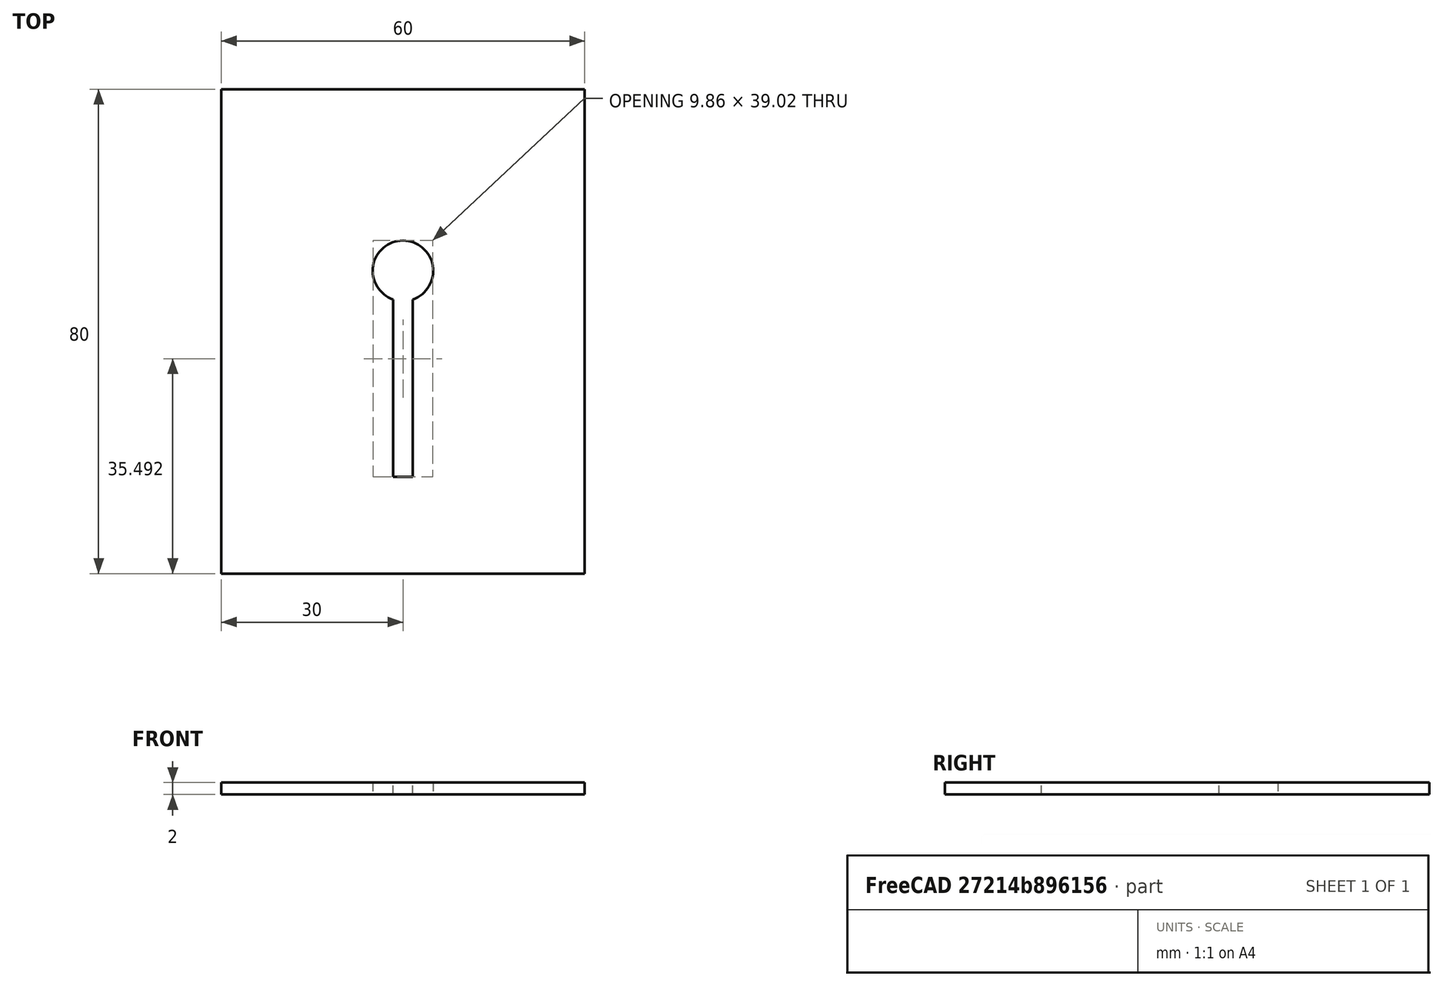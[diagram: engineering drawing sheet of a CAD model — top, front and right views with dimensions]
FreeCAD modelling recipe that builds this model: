
FCSTD DOCUMENT  (FreeCAD 0.15R4671 (Git))
Label: example 3
License: All rights reserved
LicenseURL: http://en.wikipedia.org/wiki/All_rights_reserved
objects: Sketcher::SketchObject×1, PartDesign::Pad×1
note: 3 computed .brp shape members not serialized (recipe doc carries the construction recipe); baked Part::Feature solids carry a one-line shape summary decoded from their .brp

FEATURE [Sketcher::SketchObject] Sketch  label="front plate sketch"
  Placement = pos=(0,0,32) rot=(0,0,1;0rad)
  sketch-geometry (8):
    g0: LineSegment StartX=-30 StartY=40 StartZ=0 EndX=30 EndY=40 EndZ=0
    g1: LineSegment StartX=30 StartY=40 StartZ=0 EndX=30 EndY=-40 EndZ=0
    g2: LineSegment StartX=30 StartY=-40 StartZ=0 EndX=-30 EndY=-40 EndZ=0
    g3: LineSegment StartX=-30 StartY=-40 StartZ=0 EndX=-30 EndY=40 EndZ=0
    g4: ArcOfCircle CenterX=0 CenterY=10 CenterZ=0 NormalX=0 NormalY=0 NormalZ=1 Radius=5 StartAngle=5.04311 EndAngle=10.6649
    g5: LineSegment StartX=1.62362 StartY=5.27096 StartZ=0 EndX=1.62362 EndY=-24.0165 EndZ=0
    g6: LineSegment StartX=1.62362 StartY=-24.0165 StartZ=0 EndX=-1.62362 EndY=-24.0165 EndZ=0
    g7: LineSegment StartX=-1.62362 StartY=-24.0165 StartZ=0 EndX=-1.62362 EndY=5.27096 EndZ=0
  constraints (23):
    c: Coincident(g0,g1)
    c: Coincident(g1,g2)
    c: Coincident(g2,g3)
    c: Coincident(g3,g0)
    c: Horizontal(g0)
    c: Horizontal(g2)
    c: Vertical(g1)
    c: Vertical(g3)
    c: Symmetric(g2,g1,g-2)
    c: Symmetric(g0,g2,g-1)
    c: DistanceY(g0,g2) = -80
    c: DistanceX(g2,g1) = 60
    c: DistanceX(g-1,g4) = 0
    c: DistanceY(g-1,g4) = 10
    c: Radius(g4) = 5
    c: Coincident(g5,g6)
    c: Coincident(g6,g7)
    c: Horizontal(g6)
    c: Vertical(g5)
    c: Vertical(g7)
    c: Symmetric(g5,g6,g-2)
    c: PointOnObject(g4,g7)
    c: Coincident(g5,g4)
FEATURE [PartDesign::Pad] Pad  label="front plate"
  Length = 2
  Length2 = 100
  Placement = pos=(0,0,32) rot=(0,0,1;0rad)
  Sketch = -> Sketch
  Type = 0
